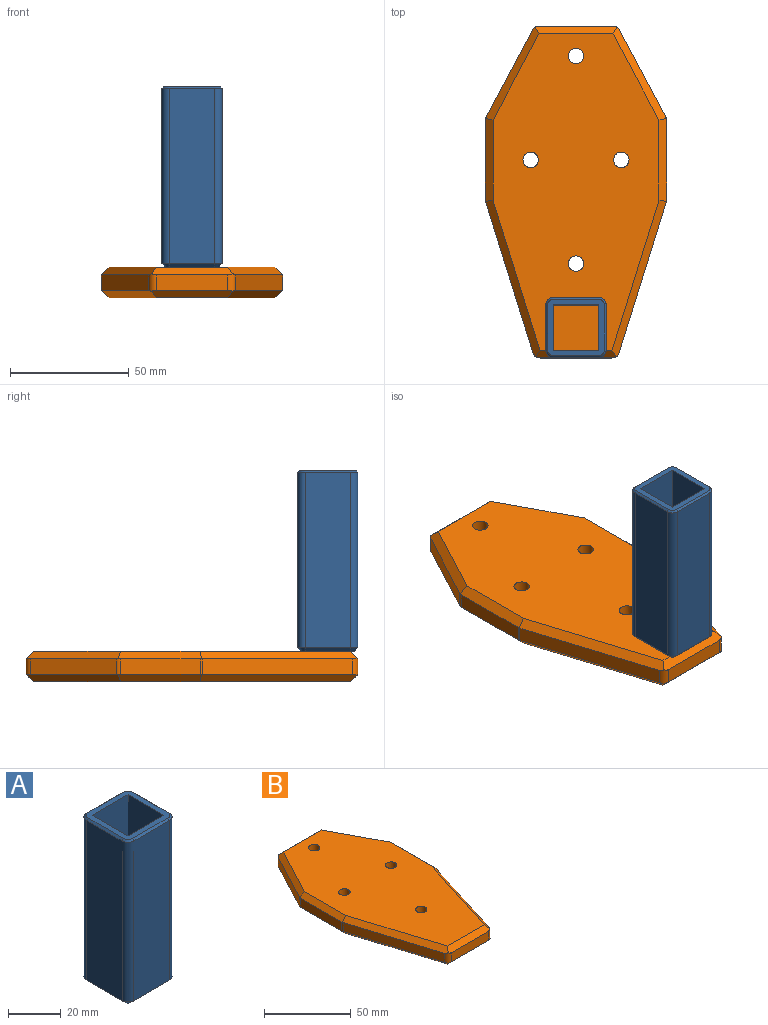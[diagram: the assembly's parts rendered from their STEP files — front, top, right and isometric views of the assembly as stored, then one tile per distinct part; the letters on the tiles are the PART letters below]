
ASSEMBLY  parts=2 mates=1
PART A: 30 faces, bbox 25.4x25.4x76.2 mm
  f0: plane 76.2x19.05mm, normal (0,-1,0), area 1451.6mm2, adj f1,f11,f12,f13
  f1: plane 76.2x19.05mm, normal (-1,0,0), area 1451.6mm2, adj f0,f2,f12,f13
  f2: plane 76.2x19.05mm, normal (0,1,0), area 1451.6mm2, adj f1,f11,f12,f13
  f3: cylinder r=3.17mm len=73.83mm, axis (0,0,-1), area 368.2mm2, adj f4,f10,f18,f28
  f4: plane 73.83x19.05mm, normal (-1,0,0), area 1406.4mm2, adj f3,f5,f16,f26
  f5: cylinder r=3.17mm len=73.83mm, axis (0,0,-1), area 368.2mm2, adj f4,f6,f14,f24
  f6: plane 73.83x19.05mm, normal (0,-1,0), area 1406.4mm2, adj f5,f7,f15,f22
  f7: cylinder r=3.17mm len=73.83mm, axis (0,0,-1), area 368.2mm2, adj f6,f8,f17,f23
  f8: plane 73.83x19.05mm, normal (1,0,0), area 1406.4mm2, adj f7,f9,f19,f25
  f9: cylinder r=3.17mm len=73.83mm, axis (0,0,-1), area 368.2mm2, adj f8,f10,f21,f27
  f10: plane 73.83x19.05mm, normal (0,1,0), area 1406.4mm2, adj f3,f9,f20,f29
  f11: plane 76.2x19.05mm, normal (1,0,0), area 1451.6mm2, adj f0,f2,f12,f13
  f12: plane 23.83x23.83mm, normal (0,0,1), area 199.8mm2, adj f0,f1,f2,f11,f22,f23,f24,f25
  f13: plane 22.23x22.23mm, normal (0,0,-1), area 128.9mm2, adj f0,f1,f2,f11,f14,f15,f16,f17
  f14: cone r=3.17mm half-angle=45deg, axis (0,0,1), area 8.4mm2, adj f5,f13,f15,f16
  f15: plane 19.05x1.59mm, normal (0,-0.71,-0.71), area 42.8mm2, adj f6,f13,f14,f17
  f16: plane 19.05x1.59mm, normal (-0.71,0,-0.71), area 42.8mm2, adj f4,f13,f14,f18
  f17: cone r=1.59mm half-angle=45deg, axis (0,0,1), area 8.4mm2, adj f7,f13,f15,f19
  f18: cone r=1.59mm half-angle=45deg, axis (0,0,1), area 8.4mm2, adj f3,f13,f16,f20
  f19: plane 19.05x1.59mm, normal (0.71,0,-0.71), area 42.8mm2, adj f8,f13,f17,f21
  f20: plane 19.05x1.59mm, normal (0,0.71,-0.71), area 42.8mm2, adj f10,f13,f18,f21
  f21: cone r=3.17mm half-angle=45deg, axis (0,0,1), area 8.4mm2, adj f9,f13,f19,f20
  f22: plane 19.05x0.79mm, normal (0,-0.71,0.71), area 21.2mm2, adj f6,f12,f23,f24
  f23: cone r=3.17mm half-angle=45deg, axis (0,0,-1), area 4.9mm2, adj f7,f12,f22,f25
  f24: cone r=2.39mm half-angle=45deg, axis (0,0,-1), area 4.9mm2, adj f5,f12,f22,f26
  f25: plane 19.05x0.79mm, normal (0.71,0,0.71), area 21.2mm2, adj f8,f12,f23,f27
  f26: plane 19.05x0.79mm, normal (-0.71,0,0.71), area 21.2mm2, adj f4,f12,f24,f28
  f27: cone r=2.39mm half-angle=45deg, axis (0,0,-1), area 4.9mm2, adj f9,f12,f25,f29
  f28: cone r=3.17mm half-angle=45deg, axis (0,0,-1), area 4.9mm2, adj f3,f12,f26,f29
  f29: plane 19.05x0.79mm, normal (0,0.71,0.71), area 21.2mm2, adj f10,f12,f27,f28
PART B: 38 faces, bbox 76.2x139.7x12.7 mm
  f0: plane 31.11x6.35mm, normal (0,1,0), area 197.5mm2, adj f14,f23,f32,f33
  f1: plane 36.49x19.37mm, normal (-0.88,0.47,0), area 262.3mm2, adj f15,f25,f33,f34
  f2: plane 33.65x6.35mm, normal (-1,0,0), area 213.7mm2, adj f17,f27,f34,f35
  f3: plane 63.21x19.8mm, normal (-0.95,-0.3,0), area 420.6mm2, adj f19,f29,f35,f36
  f4: plane 30.26x6.35mm, normal (0,-1,0), area 192.1mm2, adj f21,f28,f36,f37
  f5: plane 63.21x19.8mm, normal (0.95,-0.3,0), area 420.6mm2, adj f20,f26,f30,f37
  f6: plane 33.65x6.35mm, normal (1,0,0), area 213.7mm2, adj f18,f24,f30,f31
  f7: plane 36.49x19.37mm, normal (0.88,0.47,0), area 262.3mm2, adj f16,f22,f31,f32
  f8: plane 133.35x69.85mm, normal (0,0,1), area 7222.5mm2, adj f10,f11,f12,f13,f22,f23,f24,f25
  f9: plane 133.35x69.85mm, normal (0,0,-1), area 7222.5mm2, adj f10,f11,f12,f13,f14,f15,f16,f17
  f10: cylinder r=3.26mm len=12.7mm, axis (0,0,-1), area 260.4mm2, adj f8,f9
  f11: cylinder r=3.26mm len=12.7mm, axis (0,0,-1), area 260.4mm2, adj f8,f9
  f12: cylinder r=3.26mm len=12.7mm, axis (0,0,-1), area 260.4mm2, adj f8,f9
  f13: cylinder r=3.26mm len=12.7mm, axis (0,0,-1), area 260.4mm2, adj f8,f9
  f14: plane 34.38x3.18mm, normal (0,0.71,-0.71), area 147.4mm2, adj f0,f9,f15,f16,f32,f33
  f15: plane 39.21x22.45mm, normal (-0.62,0.33,-0.71), area 191.1mm2, adj f1,f9,f14,f17,f33,f34
  f16: plane 39.21x22.45mm, normal (0.62,0.33,-0.71), area 191.1mm2, adj f7,f9,f14,f18,f31,f32
  f17: plane 34.91x3.19mm, normal (-0.71,0,-0.71), area 153.9mm2, adj f2,f9,f15,f19,f34,f35
  f18: plane 34.91x3.19mm, normal (0.71,0,-0.71), area 153.9mm2, adj f6,f9,f16,f20,f30,f31
  f19: plane 65.79x22.95mm, normal (-0.67,-0.21,-0.71), area 303mm2, adj f3,f9,f17,f21,f35,f36
  f20: plane 65.79x22.95mm, normal (0.67,-0.21,-0.71), area 303mm2, adj f5,f9,f18,f21,f30,f37
  f21: plane 34.02x3.18mm, normal (0,-0.71,-0.71), area 144.9mm2, adj f4,f9,f19,f20,f36,f37
  f22: plane 39.21x22.45mm, normal (0.62,0.33,0.71), area 191.1mm2, adj f7,f8,f23,f24,f31,f32
  f23: plane 34.38x3.18mm, normal (0,0.71,0.71), area 147.4mm2, adj f0,f8,f22,f25,f32,f33
  f24: plane 34.91x3.19mm, normal (0.71,0,0.71), area 153.9mm2, adj f6,f8,f22,f26,f30,f31
  f25: plane 39.21x22.45mm, normal (-0.62,0.33,0.71), area 191.1mm2, adj f1,f8,f23,f27,f33,f34
  f26: plane 65.79x22.95mm, normal (0.67,-0.21,0.71), area 303mm2, adj f5,f8,f24,f28,f30,f37
  f27: plane 34.91x3.19mm, normal (-0.71,0,0.71), area 153.9mm2, adj f2,f8,f25,f29,f34,f35
  f28: plane 34.02x3.18mm, normal (0,-0.71,0.71), area 144.9mm2, adj f4,f8,f26,f29,f36,f37
  f29: plane 65.79x22.95mm, normal (-0.67,-0.21,0.71), area 303mm2, adj f3,f8,f27,f28,f35,f36
  f30: cylinder r=3.17mm len=6.42mm, axis (0,0,-1), area 6.2mm2, adj f5,f6,f18,f20,f24,f26
  f31: cylinder r=3.17mm len=6.54mm, axis (0,0,1), area 9.9mm2, adj f6,f7,f16,f18,f22,f24
  f32: cylinder r=3.17mm len=7.26mm, axis (0,0,-1), area 22.9mm2, adj f0,f7,f14,f16,f22,f23
  f33: cylinder r=3.17mm len=7.26mm, axis (0,0,1), area 22.9mm2, adj f0,f1,f14,f15,f23,f25
  f34: cylinder r=3.17mm len=6.54mm, axis (0,0,1), area 9.9mm2, adj f1,f2,f15,f17,f25,f27
  f35: cylinder r=3.17mm len=6.42mm, axis (0,0,1), area 6.2mm2, adj f2,f3,f17,f19,f27,f29
  f36: cylinder r=3.17mm len=7.58mm, axis (0,0,-1), area 27.2mm2, adj f3,f4,f19,f21,f28,f29
  f37: cylinder r=3.17mm len=7.58mm, axis (0,0,-1), area 27.2mm2, adj f4,f5,f20,f21,f26,f28
PLACE A t=(73.16,-1.77,26.06)mm
PLACE B t=(73.16,55.38,13.36)mm
MATE fastened A.f13 <-> B.f8  axis (0,0,-1) through (73.16,-1.77,26.06)mm
